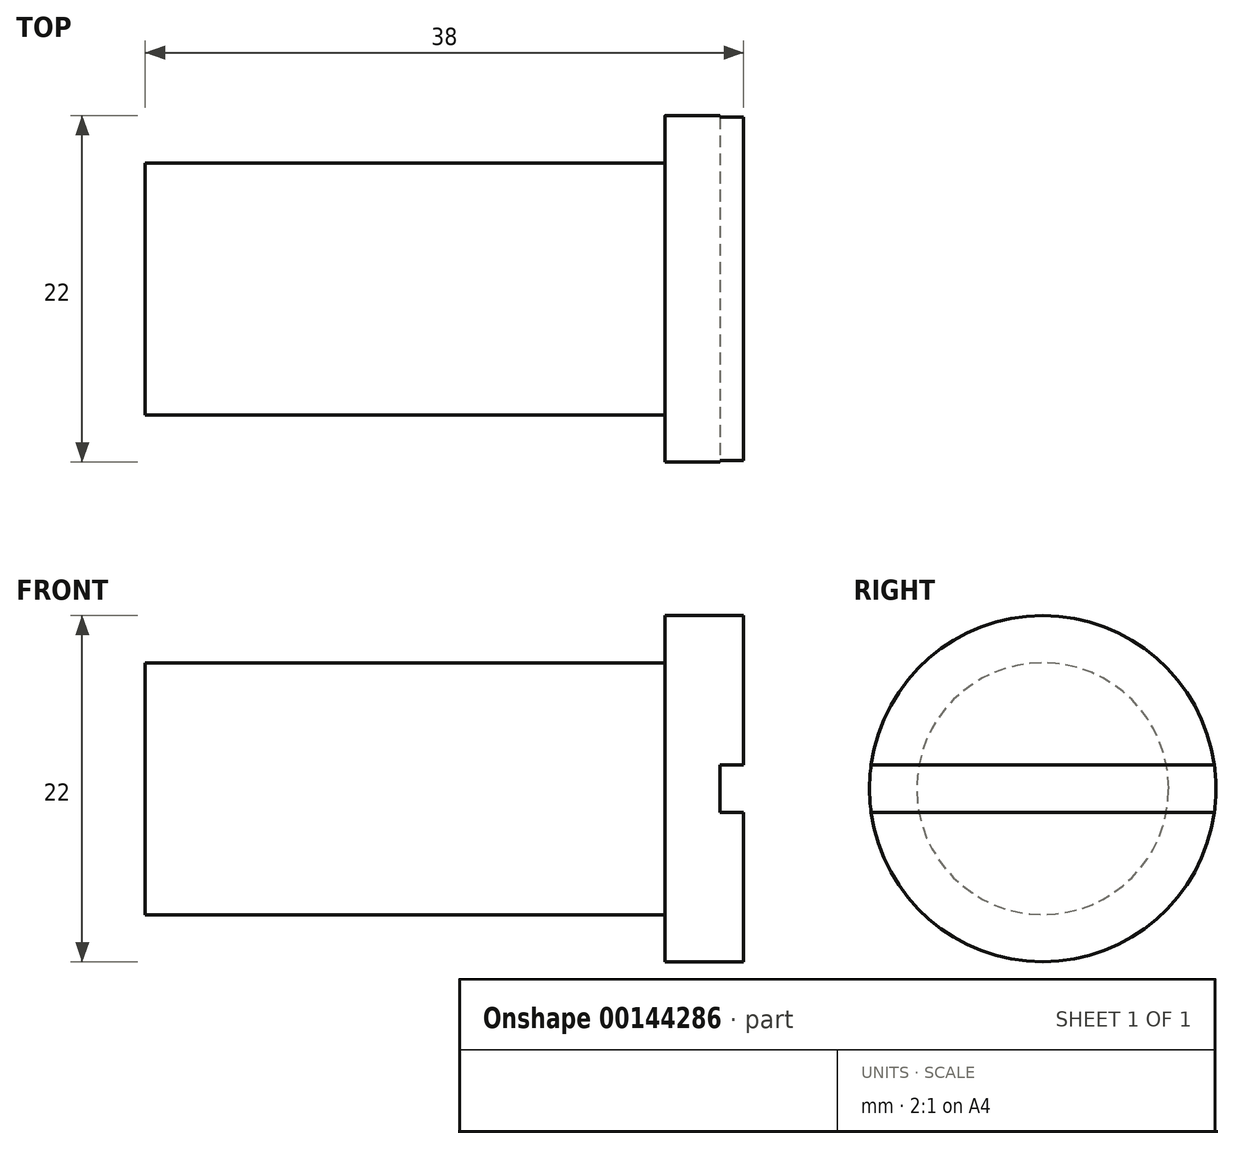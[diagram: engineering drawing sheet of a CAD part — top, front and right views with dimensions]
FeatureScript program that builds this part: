
annotation { "Feature Type Name" : "Feature", "Feature Type Description" : "" }
export const myFeature = defineFeature(function(context is Context, id is Id, definition is map)
    precondition{}
    {
        {
            var Q0;
            Q0=qCreatedBy(makeId("Right.planeOp"),FACE);
            var sketch = newSketch(context, id + "F0", { "sketchPlane" : qUnion([Q0])});
            skCircle(sketch, "E0", {"center": v(0, 0) * mm, "radius": 11 * mm});
            skLineSegment(sketch, "E1", {"start": v(-10.9, -1.5) * mm, "end": v(10.9, -1.5) * mm});
            skLineSegment(sketch, "E2", {"start": v(10.9, 1.5) * mm, "end": v(-10.9, 1.5) * mm});
            skSolve(sketch);
        }
        {
            var Q0;
            Q0 = qSketchRegion(id + "F0", true);
            extrude(context, id + "F1", {"entities" : qUnion([Q0]), "depth" : 5 * mm});
        }
        {
            var Q0;
            Q0=makeQuery(id+"F1.opExtrude","CAP_FACE",FACE,{"disambiguationData":[OSD([sQuery(id+"F0.wireOp",EDGE,"E0")])],"isStart":false});
            var sketch = newSketch(context, id + "F2", { "sketchPlane" : qUnion([Q0])});
            skLineSegment(sketch, "E3.0", {"start": v(10.9, 1.5) * mm, "end": v(-10.9, 1.5) * mm});
            skLineSegment(sketch, "E4.0", {"start": v(-10.9, -1.5) * mm, "end": v(10.9, -1.5) * mm});
            skArc(sketch, "E5.0", {"start": v(-10.9, 1.5) * mm, "mid": v(-11, 0) * mm, "end": v(-10.9, -1.5) * mm});
            skArc(sketch, "E6.trimOffspring", {"start": v(10.9, -1.5) * mm, "mid": v(11, 0) * mm, "end": v(10.9, 1.5) * mm});
            skSolve(sketch);
        }
        {
            var Q0;
            Q0 = qSketchRegion(id + "F2", true);
            extrude(context, id + "F3", {"entities" : qUnion([Q0]), "operationType" : NewBodyOperationType.REMOVE, "oppositeDirection" : true, "depth" : 1.5 * mm});
        }
        {
            var Q0;
            {var subQ0=sQuery(id+"F0.wireOp",EDGE,"E2");Q0=makeQuery(id+"F0.imprint","IMPRINT",FACE,{"disambiguationData":[TD([[makeQuery(id+"F0.imprint","IMPRINT",EDGE,{"derivedFrom":subQ0}),-1.0]])]});}
            var sketch = newSketch(context, id + "F4", { "sketchPlane" : qUnion([Q0])});
            skCircle(sketch, "E7", {"center": v(0, 0) * mm, "radius": 8 * mm});
            skSolve(sketch);
        }
        {
            var Q0;
            Q0 = qSketchRegion(id + "F4", true);
            extrude(context, id + "F5", {"entities" : qUnion([Q0]), "operationType" : NewBodyOperationType.ADD, "oppositeDirection" : true, "depth" : 33 * mm});
        }
    });
